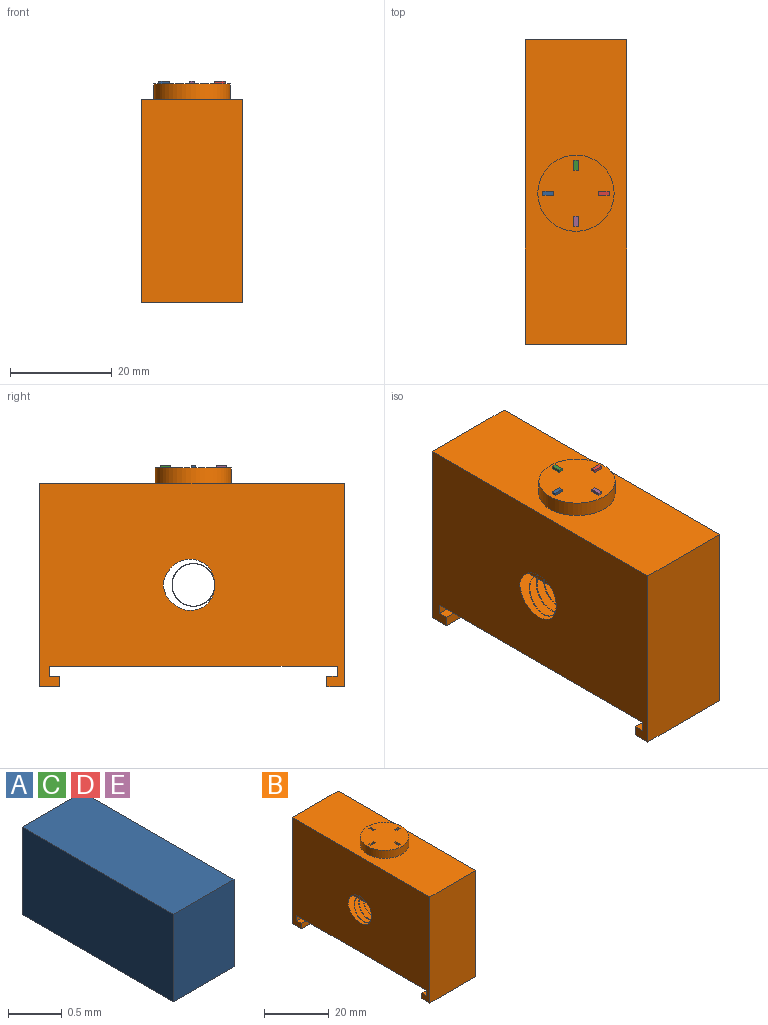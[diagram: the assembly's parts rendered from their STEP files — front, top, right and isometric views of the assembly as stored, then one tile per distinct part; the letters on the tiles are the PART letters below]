
ASSEMBLY  parts=5 mates=1
PART A: 6 faces, bbox 0.8x2x1 mm
  f0: plane 2x1mm, normal (-1,0,0), area 2mm2, adj f1,f3,f4,f5
  f1: plane 1x0.8mm, normal (0,-1,0), area 0.8mm2, adj f0,f2,f4,f5
  f2: plane 2x1mm, normal (1,0,0), area 2mm2, adj f1,f3,f4,f5
  f3: plane 1x0.8mm, normal (0,1,0), area 0.8mm2, adj f0,f2,f4,f5
  f4: plane 2x0.8mm, normal (0,0,1), area 1.6mm2, adj f0,f1,f2,f3
  f5: plane 2x0.8mm, normal (0,0,-1), area 1.6mm2, adj f0,f1,f2,f3
PART B: 37 faces, bbox 20x60x43 mm
  f0: plane 60x40mm, normal (1,0,0), area 2102.5mm2, adj f2,f3,f4,f5,f6,f7,f8,f9
  f1: plane 60x40mm, normal (-1,0,0), area 2102.5mm2, adj f2,f3,f4,f5,f6,f7,f8,f9
  f2: plane 20x3.46mm, normal (0,0,-1), area 69.1mm2, adj f0,f1,f4,f7
  f3: plane 60x20mm, normal (0,0,1), area 1023.3mm2, adj f0,f1,f4,f6,f15
  f4: plane 40x20mm, normal (0,-1,0), area 800mm2, adj f0,f1,f2,f3
  f5: plane 20x4mm, normal (0,0,-1), area 80mm2, adj f0,f1,f6,f8
  f6: plane 40x20mm, normal (0,1,0), area 800mm2, adj f0,f1,f3,f5
  f7: plane 20x2mm, normal (0,1,0), area 40mm2, adj f0,f1,f2,f13
  f8: plane 20x2mm, normal (0,-1,0), area 40mm2, adj f0,f1,f5,f9
  f9: plane 20x2mm, normal (0,0,1), area 40mm2, adj f0,f1,f8,f10
  f10: plane 20x2mm, normal (0,-1,0), area 40mm2, adj f0,f1,f9,f11
  f11: plane 56.54x20mm, normal (0,0,-1), area 1130.9mm2, adj f0,f1,f10,f12
  f12: plane 20x2mm, normal (0,1,0), area 40mm2, adj f0,f1,f11,f13
  f13: plane 20x2mm, normal (0,0,1), area 40mm2, adj f0,f1,f7,f12
  f14: cylinder r=4.2mm len=20mm, axis (1,0,0), area 11mm2, adj f0,f1
  f15: cylinder r=7.5mm len=15mm, axis (0,0,-1), area 141.4mm2, adj f3,f16
  f16: plane 15x15mm, normal (0,0,1), area 170.3mm2, adj f15,f17,f18,f19,f20,f22,f23,f24
  f17: plane 2x0.5mm, normal (0,-1,0), area 1mm2, adj f16,f18,f20,f21
  f18: plane 0.8x0.5mm, normal (1,0,0), area 0.4mm2, adj f16,f17,f19,f21
  f19: plane 2x0.5mm, normal (0,1,0), area 1mm2, adj f16,f18,f20,f21
  f20: plane 0.8x0.5mm, normal (-1,0,0), area 0.4mm2, adj f16,f17,f19,f21
  f21: plane 2x0.8mm, normal (0,0,1), area 1.6mm2, adj f17,f18,f19,f20
  f22: plane 2x0.5mm, normal (-1,0,0), area 1mm2, adj f16,f23,f25,f26
  f23: plane 0.8x0.5mm, normal (0,-1,0), area 0.4mm2, adj f16,f22,f24,f26
  f24: plane 2x0.5mm, normal (1,0,0), area 1mm2, adj f16,f23,f25,f26
  f25: plane 0.8x0.5mm, normal (0,1,0), area 0.4mm2, adj f16,f22,f24,f26
  f26: plane 2x0.8mm, normal (0,0,1), area 1.6mm2, adj f22,f23,f24,f25
  f27: plane 2x0.5mm, normal (0,1,0), area 1mm2, adj f16,f28,f30,f31
  f28: plane 0.8x0.5mm, normal (-1,0,0), area 0.4mm2, adj f16,f27,f29,f31
  f29: plane 2x0.5mm, normal (0,-1,0), area 1mm2, adj f16,f28,f30,f31
  f30: plane 0.8x0.5mm, normal (1,0,0), area 0.4mm2, adj f16,f27,f29,f31
  f31: plane 2x0.8mm, normal (0,0,1), area 1.6mm2, adj f27,f28,f29,f30
  f32: plane 2x0.5mm, normal (1,0,0), area 1mm2, adj f16,f33,f35,f36
  f33: plane 0.8x0.5mm, normal (0,1,0), area 0.4mm2, adj f16,f32,f34,f36
  f34: plane 2x0.5mm, normal (-1,0,0), area 1mm2, adj f16,f33,f35,f36
  f35: plane 0.8x0.5mm, normal (0,-1,0), area 0.4mm2, adj f16,f32,f34,f36
  f36: plane 2x0.8mm, normal (0,0,1), area 1.6mm2, adj f32,f33,f34,f35
PART C: same geometry as A
PART D: same geometry as A
PART E: same geometry as A
PLACE A rot(axis=(0,0,1),90deg) t=(-70,70,0)mm
PLACE B at identity fixed
PLACE C at identity
PLACE D rot(axis=(0,0,-1),90deg) t=(-70,-70,0)mm
PLACE E rot(axis=(0,0,1),180deg) t=(-140,0,0)mm
MATE fastened B.f36 <-> C.f5  axis (0,0,1) through (-70,5.5,42.5)mm
